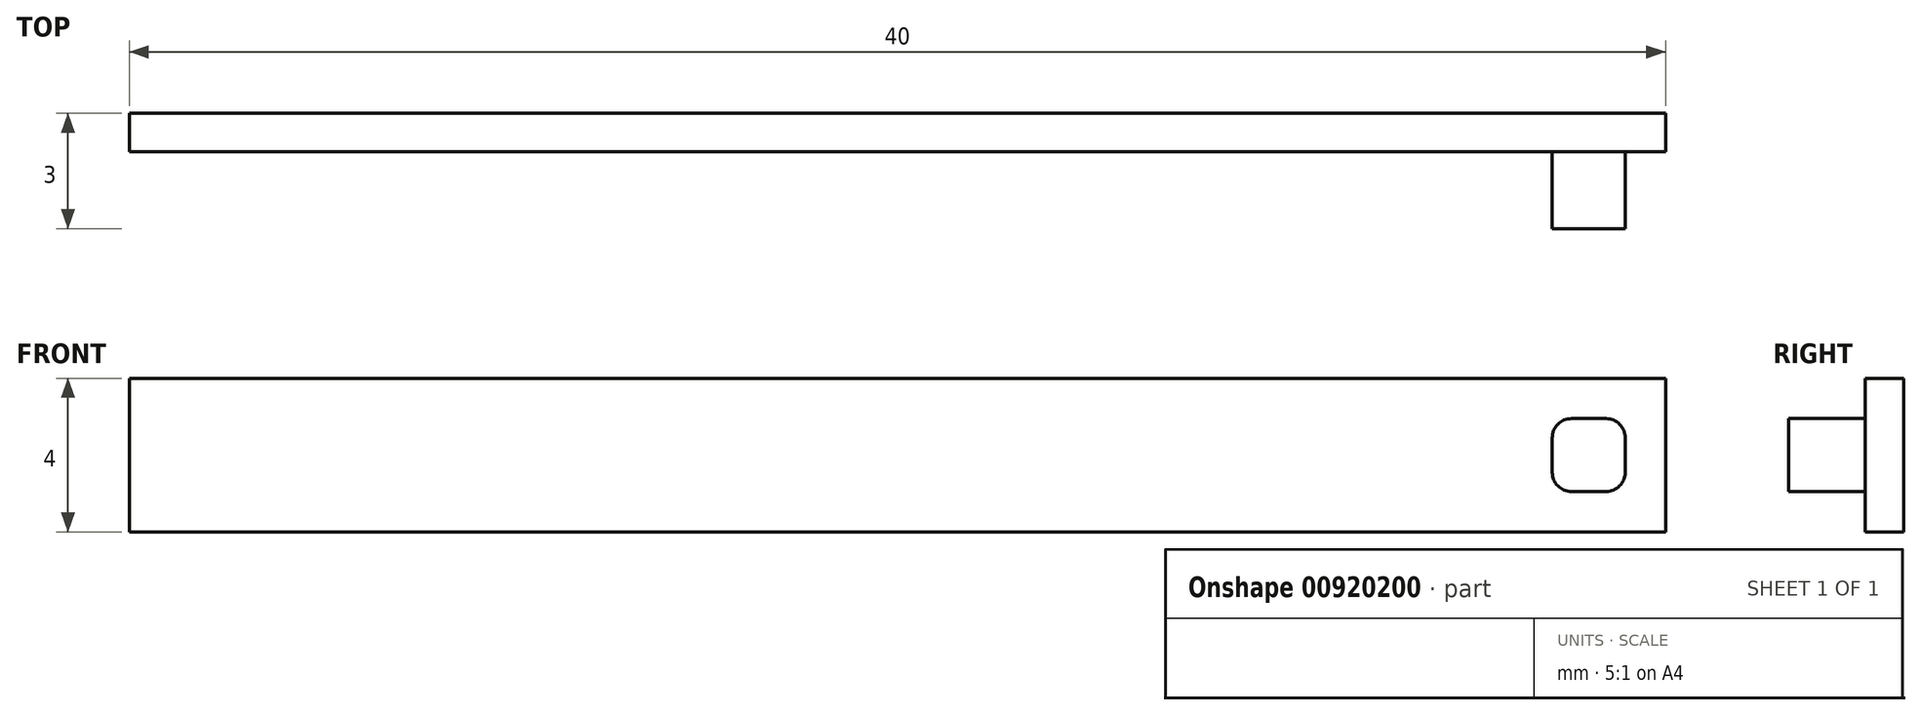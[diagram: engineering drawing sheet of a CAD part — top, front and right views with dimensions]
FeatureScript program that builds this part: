
annotation { "Feature Type Name" : "Feature", "Feature Type Description" : "" }
export const myFeature = defineFeature(function(context is Context, id is Id, definition is map)
    precondition{}
    {
        {
            var Q0;
            Q0=qCreatedBy(makeId("Front.planeOp"),FACE);
            var sketch = newSketch(context, id + "F0", { "sketchPlane" : qUnion([Q0])});
            skLineSegment(sketch, "E0.bottom", {"start": v(20, -2) * mm, "end": v(-20, -2) * mm});
            skLineSegment(sketch, "E0.top", {"start": v(20, 2) * mm, "end": v(-20, 2) * mm});
            skLineSegment(sketch, "E0.left", {"start": v(20, -2) * mm, "end": v(20, 2) * mm});
            skLineSegment(sketch, "E0.right", {"start": v(-20, -2) * mm, "end": v(-20, 2) * mm});
            skPoint(sketch, "E0.middle", {"position": v(0, 0) * mm});
            skLineSegment(sketch, "E1.bottom", {"start": v(18.9, -0.95) * mm, "end": v(17, -0.95) * mm});
            skLineSegment(sketch, "E1.top", {"start": v(18.9, 0.95) * mm, "end": v(17, 0.95) * mm});
            skLineSegment(sketch, "E1.left", {"start": v(18.9, -0.95) * mm, "end": v(18.9, 0.95) * mm});
            skLineSegment(sketch, "E1.right", {"start": v(17, -0.95) * mm, "end": v(17, 0.95) * mm});
            skPoint(sketch, "E1.middle", {"position": v(17.95, 0) * mm});
            skSolve(sketch);
        }
        {
            var Q0;
            Q0 = qSketchRegion(id + "F0", true);
            var Q1;
            Q1=makeQuery(id+"F0.imprint","IMPRINT",FACE,{"disambiguationData":[TD([[makeQuery(id+"F0.imprint","IMPRINT",EDGE,{"derivedFrom":sQuery(id+"F0.wireOp",EDGE,"E1.bottom")}),-1.0]])]});
            extrude(context, id + "F1", {"entities" : qUnion([Q0, Q1]), "depth" : 1 * mm, "offsetDistance" : 25 * mm});
        }
        {
            var Q0;
            Q0=makeQuery(id+"F1.opExtrude","CAP_FACE",FACE,{"disambiguationData":[OSD([sQuery(id+"F0.wireOp",EDGE,"E0.bottom"),sQuery(id+"F0.wireOp",EDGE,"E0.top"),sQuery(id+"F0.wireOp",EDGE,"E0.left"),sQuery(id+"F0.wireOp",EDGE,"E0.right")])],"isStart":false});
            var sketch = newSketch(context, id + "F2", { "sketchPlane" : qUnion([Q0])});
            skLineSegment(sketch, "E2.bottom", {"start": v(18.95, -0.95) * mm, "end": v(17.05, -0.95) * mm});
            skLineSegment(sketch, "E2.top", {"start": v(18.95, 0.95) * mm, "end": v(17.05, 0.95) * mm});
            skLineSegment(sketch, "E2.left", {"start": v(18.95, -0.95) * mm, "end": v(18.95, 0.95) * mm});
            skLineSegment(sketch, "E2.right", {"start": v(17.05, -0.95) * mm, "end": v(17.05, 0.95) * mm});
            skPoint(sketch, "E2.middle", {"position": v(18, 0) * mm});
            skSolve(sketch);
        }
        {
            var Q0;
            Q0=makeQuery(id+"F2.imprint","IMPRINT",FACE,{"disambiguationData":[TD([[makeQuery(id+"F2.imprint","IMPRINT",EDGE,{"derivedFrom":sQuery(id+"F2.wireOp",EDGE,"E2.bottom")}),-1.0]])]});
            extrude(context, id + "F3", {"entities" : qUnion([Q0]), "operationType" : NewBodyOperationType.ADD, "depth" : 2 * mm, "offsetDistance" : 25 * mm});
        }
        {
            var Q0;
            Q0=makeQuery(id+"F3.opExtrude","SWEPT_EDGE",EDGE,{"disambiguationData":[OSD([sQuery(id+"F2.wireOp",EDGE,"E2.top"),sQuery(id+"F2.wireOp",EDGE,"E2.left")])]});
            var Q1;
            Q1=makeQuery(id+"F3.opExtrude","SWEPT_EDGE",EDGE,{"disambiguationData":[OSD([sQuery(id+"F2.wireOp",EDGE,"E2.top"),sQuery(id+"F2.wireOp",EDGE,"E2.right")])]});
            var Q2;
            Q2=makeQuery(id+"F3.opExtrude","SWEPT_EDGE",EDGE,{"disambiguationData":[OSD([sQuery(id+"F2.wireOp",EDGE,"E2.bottom"),sQuery(id+"F2.wireOp",EDGE,"E2.left")])]});
            var Q3;
            Q3=makeQuery(id+"F3.opExtrude","SWEPT_EDGE",EDGE,{"disambiguationData":[OSD([sQuery(id+"F2.wireOp",EDGE,"E2.bottom"),sQuery(id+"F2.wireOp",EDGE,"E2.right")])]});
            fillet(context, id + "F4", {"entities" : qUnion([Q0, Q1, Q2, Q3]), "radius" : 0.5 * mm, "tangentPropagation" : true, "allowEdgeOverflow" : false});
        }
    });
